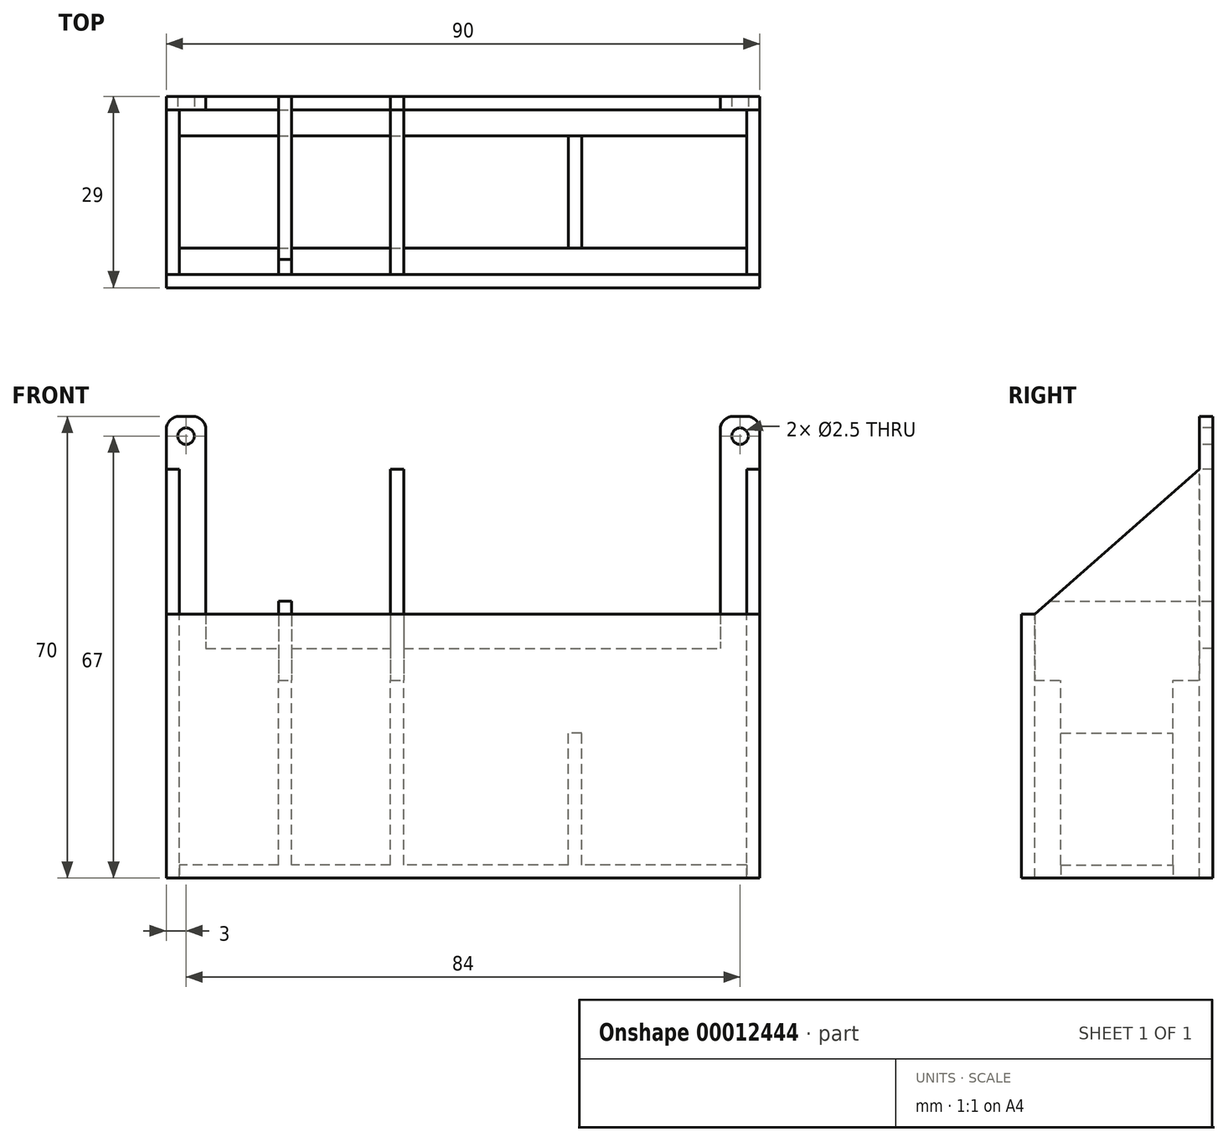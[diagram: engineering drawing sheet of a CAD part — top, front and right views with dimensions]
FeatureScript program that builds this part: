
annotation { "Feature Type Name" : "Feature", "Feature Type Description" : "" }
export const myFeature = defineFeature(function(context is Context, id is Id, definition is map)
    precondition{}
    {
        {
            var Q0;
            Q0=qCreatedBy(makeId("Front.planeOp"),FACE);
            var sketch = newSketch(context, id + "F0", { "sketchPlane" : qUnion([Q0])});
            skLineSegment(sketch, "E0.bottom", {"start": v(0, 0) * mm, "end": v(-90, 0) * mm});
            skLineSegment(sketch, "E0.top", {"start": v(-2, 70) * mm, "end": v(-88, 70) * mm});
            skLineSegment(sketch, "E0.left", {"start": v(0, 0) * mm, "end": v(0, 68) * mm});
            skLineSegment(sketch, "E0.right", {"start": v(-90, 0) * mm, "end": v(-90, 68) * mm});
            skPoint(sketch, "E1.visualSharp", {"position": v(0, 70) * mm});
            skArc(sketch, "E1.filletArc", {"start": v(0, 68) * mm, "mid": v(-0.59, 69.41) * mm, "end": v(-2, 70) * mm});
            skPoint(sketch, "E2.visualSharp", {"position": v(-90, 70) * mm});
            skArc(sketch, "E2.filletArc", {"start": v(-88, 70) * mm, "mid": v(-89.41, 69.41) * mm, "end": v(-90, 68) * mm});
            skSolve(sketch);
        }
        {
            var Q0;
            Q0=qSketchRegion(id+"F0",true);
            extrude(context, id + "F1", {"entities" : qUnion([Q0]), "oppositeDirection" : true, "depth" : 2 * mm});
        }
        {
            var Q0;
            Q0=makeQuery(id+"F1.opExtrude","CAP_FACE",FACE,{"disambiguationData":[OSD([sQuery(id+"F0.wireOp",EDGE,"E0.bottom"),sQuery(id+"F0.wireOp",EDGE,"E0.top"),sQuery(id+"F0.wireOp",EDGE,"E0.left"),sQuery(id+"F0.wireOp",EDGE,"E0.right")])],"isStart":true});
            var sketch = newSketch(context, id + "F2", { "sketchPlane" : qUnion([Q0])});
            skLineSegment(sketch, "E3.bottom", {"start": v(-90, 2) * mm, "end": v(0, 2) * mm});
            skLineSegment(sketch, "E3.top", {"start": v(-90, 0) * mm, "end": v(0, 0) * mm});
            skLineSegment(sketch, "E3.left", {"start": v(-90, 2) * mm, "end": v(-90, 0) * mm});
            skLineSegment(sketch, "E3.right", {"start": v(0, 2) * mm, "end": v(0, 0) * mm});
            skLineSegment(sketch, "E4.bottom", {"start": v(0, 2) * mm, "end": v(-2, 2) * mm});
            skLineSegment(sketch, "E4.top", {"start": v(0, 62) * mm, "end": v(-2, 62) * mm});
            skLineSegment(sketch, "E4.left", {"start": v(0, 2) * mm, "end": v(0, 62) * mm});
            skLineSegment(sketch, "E4.right", {"start": v(-2, 2) * mm, "end": v(-2, 62) * mm});
            skLineSegment(sketch, "E5.bottom", {"start": v(-90, 2) * mm, "end": v(-88, 2) * mm});
            skLineSegment(sketch, "E5.top", {"start": v(-90, 62) * mm, "end": v(-88, 62) * mm});
            skLineSegment(sketch, "E5.left", {"start": v(-90, 2) * mm, "end": v(-90, 62) * mm});
            skLineSegment(sketch, "E5.right", {"start": v(-88, 2) * mm, "end": v(-88, 62) * mm});
            skLineSegment(sketch, "E6.bottom", {"start": v(-73, 42) * mm, "end": v(-71, 42) * mm});
            skLineSegment(sketch, "E6.top", {"start": v(-73, 2) * mm, "end": v(-71, 2) * mm});
            skLineSegment(sketch, "E6.left", {"start": v(-73, 42) * mm, "end": v(-73, 2) * mm});
            skLineSegment(sketch, "E6.right", {"start": v(-71, 42) * mm, "end": v(-71, 2) * mm});
            skLineSegment(sketch, "E7.bottom", {"start": v(-56, 62) * mm, "end": v(-54, 62) * mm});
            skLineSegment(sketch, "E7.top", {"start": v(-56, 2) * mm, "end": v(-54, 2) * mm});
            skLineSegment(sketch, "E7.left", {"start": v(-56, 62) * mm, "end": v(-56, 2) * mm});
            skLineSegment(sketch, "E7.right", {"start": v(-54, 62) * mm, "end": v(-54, 2) * mm});
            skLineSegment(sketch, "E8.bottom", {"start": v(-29, 22) * mm, "end": v(-27, 22) * mm});
            skLineSegment(sketch, "E8.top", {"start": v(-29, 2) * mm, "end": v(-27, 2) * mm});
            skLineSegment(sketch, "E8.left", {"start": v(-29, 22) * mm, "end": v(-29, 2) * mm});
            skLineSegment(sketch, "E8.right", {"start": v(-27, 22) * mm, "end": v(-27, 2) * mm});
            skSolve(sketch);
        }
        {
            var Q0;
            Q0=qSketchRegion(id+"F2",true);
            extrude(context, id + "F3", {"entities" : qUnion([Q0]), "operationType" : NewBodyOperationType.ADD, "depth" : 25 * mm});
        }
        {
            var Q0;
            Q0=makeQuery(id+"F3.opExtrude","CAP_FACE",FACE,{"disambiguationData":[OSD([sQuery(id+"F2.wireOp",EDGE,"E3.bottom"),sQuery(id+"F2.wireOp",EDGE,"E3.top"),sQuery(id+"F2.wireOp",EDGE,"E3.left"),sQuery(id+"F2.wireOp",EDGE,"E3.right"),sQuery(id+"F2.wireOp",EDGE,"E4.top"),sQuery(id+"F2.wireOp",EDGE,"E4.left"),sQuery(id+"F2.wireOp",EDGE,"E4.right"),sQuery(id+"F2.wireOp",EDGE,"E5.top"),sQuery(id+"F2.wireOp",EDGE,"E5.left"),sQuery(id+"F2.wireOp",EDGE,"E5.right"),sQuery(id+"F2.wireOp",EDGE,"E6.bottom"),sQuery(id+"F2.wireOp",EDGE,"E6.left"),sQuery(id+"F2.wireOp",EDGE,"E6.right"),sQuery(id+"F2.wireOp",EDGE,"aab91a0f-a239-46ca-9d51-01bc5ff683ef.bottom"),sQuery(id+"F2.wireOp",EDGE,"aab91a0f-a239-46ca-9d51-01bc5ff683ef.left"),sQuery(id+"F2.wireOp",EDGE,"aab91a0f-a239-46ca-9d51-01bc5ff683ef.right"),sQuery(id+"F2.wireOp",EDGE,"E7.bottom"),sQuery(id+"F2.wireOp",EDGE,"E7.left"),sQuery(id+"F2.wireOp",EDGE,"E7.right"),sQuery(id+"F2.wireOp",EDGE,"E8.bottom"),sQuery(id+"F2.wireOp",EDGE,"E8.left"),sQuery(id+"F2.wireOp",EDGE,"E8.right")])],"isStart":false});
            var sketch = newSketch(context, id + "F4", { "sketchPlane" : qUnion([Q0])});
            skLineSegment(sketch, "E9.bottom", {"start": v(-90, 0) * mm, "end": v(0, 0) * mm});
            skLineSegment(sketch, "E9.top", {"start": v(-90, 40) * mm, "end": v(0, 40) * mm});
            skLineSegment(sketch, "E9.left", {"start": v(-90, 0) * mm, "end": v(-90, 40) * mm});
            skLineSegment(sketch, "E9.right", {"start": v(0, 0) * mm, "end": v(0, 40) * mm});
            skSolve(sketch);
        }
        {
            var Q0;
            Q0=qSketchRegion(id+"F4",true);
            extrude(context, id + "F5", {"entities" : qUnion([Q0]), "operationType" : NewBodyOperationType.ADD, "depth" : 2 * mm});
        }
        {
            var Q0;
            Q0=makeQuery(id+"F1.opExtrude","CAP_FACE",FACE,{"disambiguationData":[OSD([sQuery(id+"F0.wireOp",EDGE,"E0.bottom"),sQuery(id+"F0.wireOp",EDGE,"E0.top"),sQuery(id+"F0.wireOp",EDGE,"E0.left"),sQuery(id+"F0.wireOp",EDGE,"E0.right")])],"isStart":true});
            var sketch = newSketch(context, id + "F6", { "sketchPlane" : qUnion([Q0])});
            skCircle(sketch, "E10", {"center": v(-87, 67) * mm, "radius": 1.25 * mm});
            skCircle(sketch, "E11", {"center": v(-3, 67) * mm, "radius": 1.25 * mm});
            skSolve(sketch);
        }
        {
            var Q0;
            Q0=qSketchRegion(id+"F6",true);
            extrude(context, id + "F7", {"entities" : qUnion([Q0]), "operationType" : NewBodyOperationType.REMOVE, "oppositeDirection" : true, "depth" : 2 * mm});
        }
        {
            var Q0;
            Q0=makeQuery(id+"F5.boolean.opBoolean","MERGE",FACE,{"derivedFrom":[makeQuery(id+"F3.boolean.opBoolean","MERGE",FACE,{"derivedFrom":[makeQuery(id+"F1.opExtrude","SWEPT_FACE",FACE,{"disambiguationData":[OSD([sQuery(id+"F0.wireOp",EDGE,"E0.right")])]}),makeQuery(id+"F3.opExtrude","SWEPT_FACE",FACE,{"disambiguationData":[OSD([sQuery(id+"F2.wireOp",EDGE,"E3.left"),sQuery(id+"F2.wireOp",EDGE,"E5.left")])]})]}),makeQuery(id+"F5.opExtrude","SWEPT_FACE",FACE,{"disambiguationData":[OSD([sQuery(id+"F4.wireOp",EDGE,"E9.left")])]})]});
            var sketch = newSketch(context, id + "F8", { "sketchPlane" : qUnion([Q0])});
            skLineSegment(sketch, "E12", {"start": v(25, 62) * mm, "end": v(25, 40) * mm});
            skLineSegment(sketch, "E13", {"start": v(25, 40) * mm, "end": v(0, 62) * mm});
            skLineSegment(sketch, "E14", {"start": v(0, 62) * mm, "end": v(25, 62) * mm});
            skSolve(sketch);
        }
        {
            var Q0;
            Q0=qSketchRegion(id+"F8",true);
            extrude(context, id + "F9", {"entities" : qUnion([Q0]), "operationType" : NewBodyOperationType.REMOVE, "oppositeDirection" : true, "depth" : 110 * mm});
        }
        {
            var Q0;
            Q0=makeQuery(id+"F5.boolean.opBoolean","MERGE",FACE,{"derivedFrom":[makeQuery(id+"F3.boolean.opBoolean","MERGE",FACE,{"derivedFrom":[makeQuery(id+"F1.opExtrude","SWEPT_FACE",FACE,{"disambiguationData":[OSD([sQuery(id+"F0.wireOp",EDGE,"E0.bottom")])]}),makeQuery(id+"F3.opExtrude","SWEPT_FACE",FACE,{"disambiguationData":[OSD([sQuery(id+"F2.wireOp",EDGE,"E3.top")])]})]}),makeQuery(id+"F5.opExtrude","SWEPT_FACE",FACE,{"disambiguationData":[OSD([sQuery(id+"F4.wireOp",EDGE,"E9.bottom")])]})]});
            var sketch = newSketch(context, id + "F10", { "sketchPlane" : qUnion([Q0])});
            skLineSegment(sketch, "E15.bottom", {"start": v(-88, 0) * mm, "end": v(-2, 0) * mm});
            skLineSegment(sketch, "E15.top", {"start": v(-88, 4) * mm, "end": v(-2, 4) * mm});
            skLineSegment(sketch, "E15.left", {"start": v(-88, 0) * mm, "end": v(-88, 4) * mm});
            skLineSegment(sketch, "E15.right", {"start": v(-2, 0) * mm, "end": v(-2, 4) * mm});
            skLineSegment(sketch, "E16.bottom", {"start": v(-88, 21) * mm, "end": v(-2, 21) * mm});
            skLineSegment(sketch, "E16.top", {"start": v(-88, 25) * mm, "end": v(-2, 25) * mm});
            skLineSegment(sketch, "E16.left", {"start": v(-88, 21) * mm, "end": v(-88, 25) * mm});
            skLineSegment(sketch, "E16.right", {"start": v(-2, 21) * mm, "end": v(-2, 25) * mm});
            skSolve(sketch);
        }
        {
            var Q0;
            Q0=qSketchRegion(id+"F10",true);
            extrude(context, id + "F11", {"entities" : qUnion([Q0]), "operationType" : NewBodyOperationType.REMOVE, "oppositeDirection" : true, "depth" : 30 * mm});
        }
        {
            var Q0;
            Q0=makeQuery(id+"F11.boolean.opBoolean","MERGE",FACE,{"derivedFrom":[makeQuery(id+"F1.opExtrude","CAP_FACE",FACE,{"disambiguationData":[OSD([sQuery(id+"F0.wireOp",EDGE,"E0.bottom"),sQuery(id+"F0.wireOp",EDGE,"E0.top"),sQuery(id+"F0.wireOp",EDGE,"E0.left"),sQuery(id+"F0.wireOp",EDGE,"E0.right"),sQuery(id+"F0.wireOp",EDGE,"E1.filletArc"),sQuery(id+"F0.wireOp",EDGE,"E2.filletArc")])],"isStart":true}),makeQuery(id+"F11.opExtrude","SWEPT_FACE",FACE,{"disambiguationData":[OSD([sQuery(id+"F10.wireOp",EDGE,"E15.bottom")])]})]});
            var sketch = newSketch(context, id + "F12", { "sketchPlane" : qUnion([Q0])});
            skLineSegment(sketch, "E17.bottom", {"start": v(-84, 70) * mm, "end": v(-6, 70) * mm});
            skLineSegment(sketch, "E17.top", {"start": v(-84, 34.81) * mm, "end": v(-6, 34.81) * mm});
            skLineSegment(sketch, "E17.left", {"start": v(-84, 68) * mm, "end": v(-84, 34.81) * mm});
            skLineSegment(sketch, "E17.right", {"start": v(-6, 68) * mm, "end": v(-6, 34.81) * mm});
            skLineSegment(sketch, "E18", {"start": v(-88, 70) * mm, "end": v(-86, 70) * mm});
            skLineSegment(sketch, "E19", {"start": v(-4, 70) * mm, "end": v(-2, 70) * mm});
            skArc(sketch, "E20.filletArc", {"start": v(-4, 70) * mm, "mid": v(-5.41, 69.41) * mm, "end": v(-6, 68) * mm});
            skArc(sketch, "E21.filletArc", {"start": v(-84, 68) * mm, "mid": v(-84.59, 69.41) * mm, "end": v(-86, 70) * mm});
            skSolve(sketch);
        }
        {
            var Q0;
            {var subQ14=sQuery(id+"F12.wireOp",EDGE,"E17.bottom");Q0=makeQuery(id+"F12.imprint","IMPRINT",FACE,{"disambiguationData":[TD([[makeQuery(id+"F12.imprint","IMPRINT",EDGE,{"derivedFrom":subQ14}),1.0]])]});}
            extrude(context, id + "F13", {"entities" : qUnion([Q0]), "operationType" : NewBodyOperationType.REMOVE, "oppositeDirection" : true, "depth" : 2 * mm});
        }
    });
